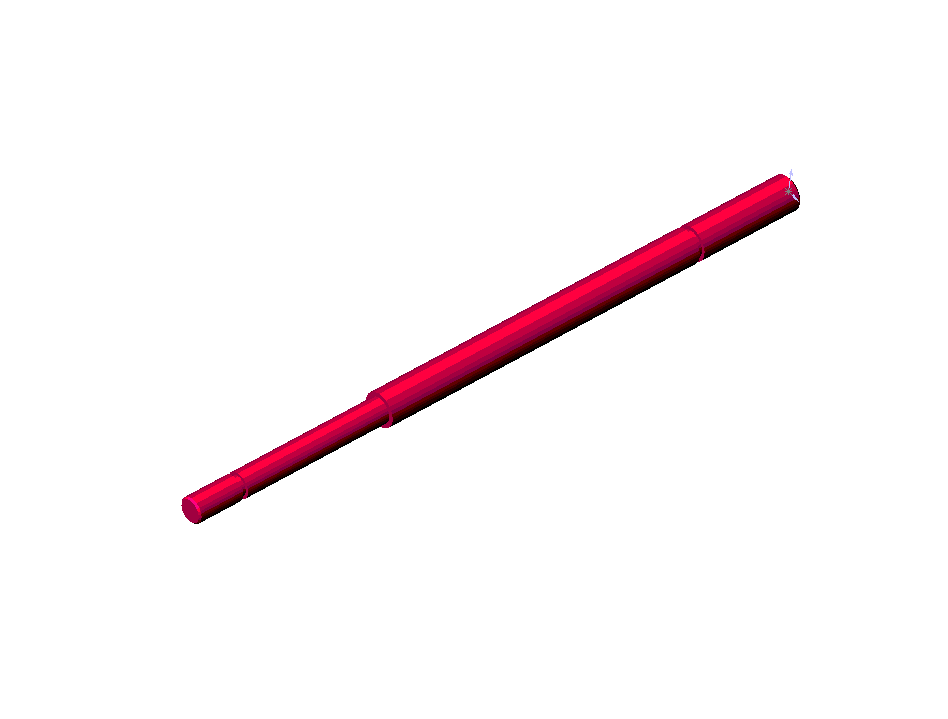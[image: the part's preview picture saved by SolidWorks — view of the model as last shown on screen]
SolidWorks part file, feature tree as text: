
SOLIDWORKS PART (.sldprt)
format: sldprt  version: not decoded by parser v0  size: 109,056 bytes
history: native  units: mm
features: plane x3, sketch x3, extrude x2, material x1, chamfer x1, cut_revolve x1 (+10 scaffold rows collapsed)
feature tree (21):
  scaffold x10  (default folders/planes/origin — collapsed)
  material  "Matériau <non spécifié>"
  plane  "Plan1"
  plane  "Plan2"
  plane  "Plan3"
  sketch  "Esquisse1"  dims[D1=4.0mm]
  extrude  "Base-Extrusion"  Depth=54mm
  sketch  "Esquisse2"  dims[D1=3.0mm]
  extrude  "Boss.-Extru.1"  Depth=25mm
  chamfer  "Chanfrein1"  Distance=0.2mm Angle=45deg
  sketch  "Esquisse3"  dims[D1=0.64mm D2=2.3mm D3=5.5mm D4=0.64mm D5=3.2mm D6=60.5mm]
  cut_revolve  "Enlèvement de matière-Révolution1"  Angle=360deg
decode coverage: 7 of 7 modeling features carry decoded parameters
note: suppression state not decoded; provenance and decode notes live in map.json
